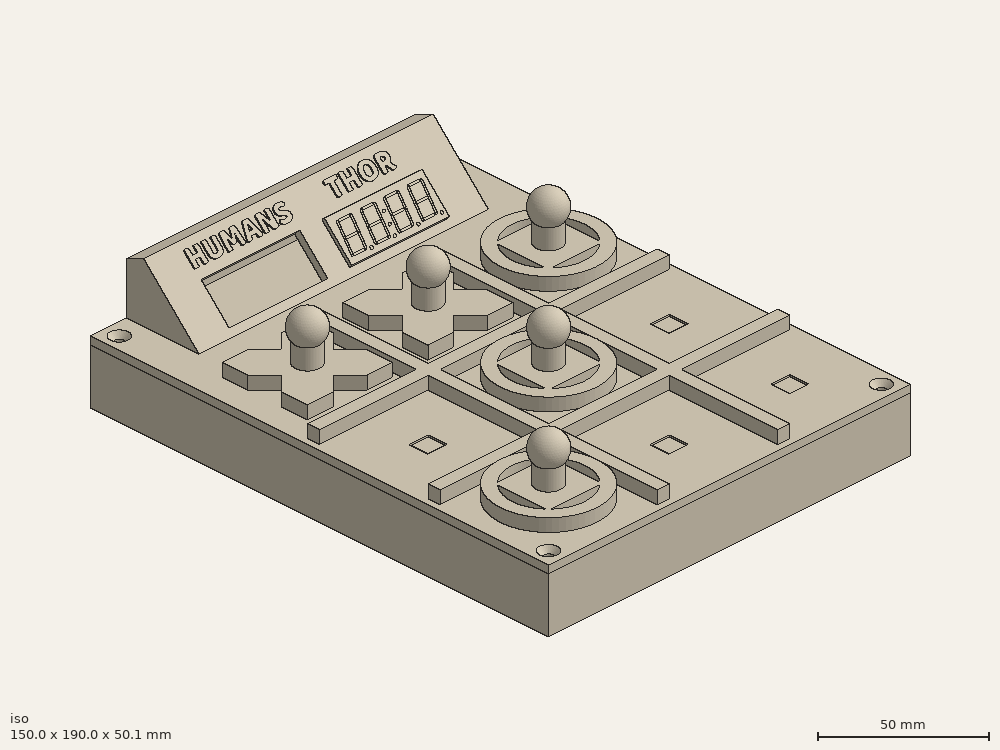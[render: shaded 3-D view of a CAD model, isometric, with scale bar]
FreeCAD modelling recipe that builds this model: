
FCSTD DOCUMENT  (FreeCAD 0.16R6707 (Git))
Label: 3enraya
License: All rights reserved
LicenseURL: http://en.wikipedia.org/wiki/All_rights_reserved
objects: Part::FeaturePython×36, Part::Feature×23, Part::MultiFuse×19, Part::Cut×14, Part::Cylinder×14, Part::Extrusion×13, Part::Box×11, Sketcher::SketchObject×3, PartDesign::Pad×3, Part::Thickness×2, Part::Chamfer×2, Part::Sphere×2, Part::Compound×2, Part::Cone×1, Part::Fillet×1, App::DocumentObjectGroup×1, Part::Prism×1, Part::Mirroring×1
note: 151 computed .brp shape members not serialized (recipe doc carries the construction recipe); baked Part::Feature solids carry a one-line shape summary decoded from their .brp

FEATURE [Part::Box] Box  label="Cube"
  Height = 14
  Length = 7
  Placement = pos=(6.5,6.5,5) rot=(0,0,1;0rad)
  Width = 7
FEATURE [Part::Box] Box001  label="Cube001"
  Height = 1.7
  Length = 20
  Placement = pos=(0,0,3.3) rot=(0,0,1;0rad)
  Width = 20
FEATURE [Part::MultiFuse] Fusion  label="Sensor"
  Shapes = -> [Box,Box001]
FEATURE [Part::Box] Box002  label="Cube002"
  Height = 3
  Length = 150
  Placement = pos=(-15,-15,16.3) rot=(0,0,1;0rad)
  Width = 190
FEATURE [Part::Box] Box003  label="Cube003"
  Height = 20
  Length = 8
  Placement = pos=(6,6,5) rot=(0,0,1;0rad)
  Width = 8
FEATURE [Part::FeaturePython] Array001  # Draft array (typed FeaturePython)
  Angle = 360
  ArrayType = 0
  Axis = (0,0,1)
  Base = -> Box003
  Center = (0,0,0)
  Fuse = false
  IntervalAxis = (0,0,0)
  IntervalX = (50,0,0)
  IntervalY = (0,50,0)
  IntervalZ = (0,0,0)
  NumberPolar = 1
  NumberX = 3
  NumberY = 3
  NumberZ = 1
FEATURE [Part::Cut] Cut
  Base = -> Box002
  Tool = -> Array001
FEATURE [Part::Box] Box004  label="Cube004"
  Height = 21.3
  Length = 150
  Placement = pos=(-15,-15,-5) rot=(0,0,1;0rad)
  Width = 190
FEATURE [Part::Thickness] Thickness
  Faces = -> Box004 [Face6]
  Intersection = false
  Join = 0
  Mode = 0
  SelfIntersection = false
  Value = -3
FEATURE [Part::Cylinder] Cylinder
  Angle = 360
  Height = 10
  Placement = pos=(18,18,0) rot=(0,0,1;0rad)
  Radius = 1
FEATURE [Part::Cylinder] Cylinder001
  Angle = 360
  Height = 10
  Placement = pos=(2,2,0) rot=(0,0,1;0rad)
  Radius = 1
FEATURE [Part::MultiFuse] Fusion001
  Shapes = -> [Cylinder001,Cylinder]
FEATURE [Part::Cut] Cut001
  Base = -> Fusion
  Tool = -> Fusion001
FEATURE [Part::FeaturePython] Array  # Draft array (typed FeaturePython)
  Angle = 360
  ArrayType = 0
  Axis = (0,0,1)
  Base = -> Cut001
  Center = (0,0,0)
  Fuse = false
  IntervalAxis = (0,0,0)
  IntervalX = (50,0,0)
  IntervalY = (0,50,0)
  IntervalZ = (0,0,0)
  NumberPolar = 1
  NumberX = 3
  NumberY = 3
  NumberZ = 1
FEATURE [Part::Cylinder] Cylinder002
  Angle = 360
  Height = 8.25
  Placement = pos=(1.11,1.11,-4.95) rot=(0,0,1;0rad)
  Radius = 1
FEATURE [Part::Cylinder] Cylinder003
  Angle = 360
  Height = 8.25
  Placement = pos=(18.89,18.89,-4.95) rot=(0,0,1;0rad)
  Radius = 1
FEATURE [Part::Cylinder] Cylinder004
  Angle = 360
  Height = 8.25
  Placement = pos=(18.89,18.89,-4.95) rot=(0,0,1;0rad)
  Radius = 3
FEATURE [Part::Cylinder] Cylinder005
  Angle = 360
  Height = 8.25
  Placement = pos=(1.11,1.11,-4.95) rot=(0,0,1;0rad)
  Radius = 3
FEATURE [Part::MultiFuse] Fusion002
  Shapes = -> [Cylinder002,Cylinder003]
FEATURE [Part::MultiFuse] Fusion003
  Shapes = -> [Cylinder005,Cylinder004]
FEATURE [Part::Box] Box005  label="Cube005"
  Height = 5
  Length = 5
  Placement = pos=(82.5,-12.5,19.3) rot=(0,0,1;0rad)
  Width = 145
FEATURE [Part::FeaturePython] Clone  label="Clone of Cube005"  # Draft clone (typed FeaturePython)
  Objects = -> [Box005]
  Placement = pos=(32.5,-12.5,19.3) rot=(0,0,1;0rad)
  Scale = (1,1,1)
FEATURE [Part::FeaturePython] Clone001  label="Clone of Cube006"  # Draft clone (typed FeaturePython)
  Objects = -> [Box005]
  Placement = pos=(132.5,82.5,19.3) rot=(0,0,1;1.5708rad)
  Scale = (1,1,1)
FEATURE [Part::FeaturePython] Clone002  label="Clone of Cube007"  # Draft clone (typed FeaturePython)
  Objects = -> [Box005]
  Placement = pos=(132.5,32.5,19.3) rot=(0,0,1;1.5708rad)
  Scale = (1,1,1)
FEATURE [Part::MultiFuse] Fusion005
  Shapes = -> [Clone002,Clone001,Clone,Box005,Cut]
FEATURE [Part::Cone] Cone
  Angle = 90
  Height = 12
  Placement = pos=(-12,-12,4.3) rot=(0,0,1;0rad)
  Radius1 = 0
  Radius2 = 10
FEATURE [Part::Box] Box006  label="Cube006"
  Height = 10
  Length = 20
  Placement = pos=(50,165,-2) rot=(0,0,1;0rad)
  Width = 10
FEATURE [Part::Fillet] Fillet
  Base = -> Box006
  Edges = 4 edges r=3: [Edge2,Edge4,Edge6,Edge8]
FEATURE [Part::FeaturePython] Clone003  label="Clone of Cone"  # Draft clone (typed FeaturePython)
  Objects = -> [Cone]
  Placement = pos=(132,-12,4.3) rot=(0,0,1;1.5708rad)
  Scale = (1,1,1)
FEATURE [Part::FeaturePython] Clone004  label="Clone of Cone001"  # Draft clone (typed FeaturePython)
  Objects = -> [Cone]
  Placement = pos=(-12,172,4.3) rot=(0,0,-1;1.5708rad)
  Scale = (1,1,1)
FEATURE [Part::FeaturePython] Clone005  label="Clone of Cone002"  # Draft clone (typed FeaturePython)
  Objects = -> [Cone]
  Placement = pos=(132,172,4.3) rot=(0,0,1;3.14159rad)
  Scale = (1,1,1)
FEATURE [Part::Cylinder] Cylinder006
  Angle = 360
  Height = 10
  Placement = pos=(-9,169,6.3) rot=(0,0,1;0rad)
  Radius = 1.6
FEATURE [Part::FeaturePython] Clone006  label="Clone of Cylinder006"  # Draft clone (typed FeaturePython)
  Objects = -> [Cylinder006]
  Placement = pos=(129,-9,6.3) rot=(0,0,1;0rad)
  Scale = (1,1,1)
FEATURE [Part::FeaturePython] Clone007  label="Clone of Cylinder007"  # Draft clone (typed FeaturePython)
  Objects = -> [Cylinder006]
  Placement = pos=(129,169,6.3) rot=(0,0,1;0rad)
  Scale = (1,1,1)
FEATURE [Part::FeaturePython] Clone008  label="Clone of Cylinder008"  # Draft clone (typed FeaturePython)
  Objects = -> [Cylinder006]
  Placement = pos=(-9,-9,6.3) rot=(0,0,1;0rad)
  Scale = (1,1,1)
FEATURE [Part::MultiFuse] Fusion007
  Shapes = -> [Clone008,Clone007,Clone006,Cylinder006]
FEATURE [Part::FeaturePython] Clone009  label="Clone of Fusion007"  # Draft clone (typed FeaturePython)
  Objects = -> [Fusion007]
  Placement = pos=(0,0,5) rot=(0,0,1;0rad)
  Scale = (1,1,1)
FEATURE [Part::Cut] Cut005
  Base = -> Fusion005
  Tool = -> Clone009
FEATURE [Part::Chamfer] Chamfer
  Base = -> Cut005
  Edges = 4 edges r=2: [Edge129,Edge146,Edge147,Edge148]
FEATURE [Part::Feature] Part__Feature  label="nano-board"
  shape: bbox 43.2 x 4.77 x 18 mm, 378 faces (baked)
FEATURE [Part::Feature] Part__Feature011  label="smt_resistor225"
  Placement = pos=(36.75,0,-12) rot=(-0.707107,0,0.707107;3.14159rad)
  shape: bbox 3.8 x 0.6 x 1.813 mm, 74 faces (baked)
FEATURE [Part::Feature] Part__Feature022  label="MINIUSBSHELL"
  Placement = pos=(38.98,1.65,-7.62) rot=(0,-1,0;1.5708rad)
  shape: bbox 9.475 x 3.822 x 11.03 mm, 243 faces (baked)
FEATURE [Part::Feature] Part__Feature023  label="MINIUSBCORE"
  Placement = pos=(32.28,1.65,-7.62) rot=(0,1,0;1.5708rad)
  shape: bbox 8.2 x 4.5 x 7.7 mm, 127 faces (baked)
FEATURE [Part::Feature] Part__Feature024  label="MINI USB CONTACT"
  Placement = pos=(33.28,1.65,-9.22) rot=(0,1,0;1.5708rad)
  shape: bbox 9.423 x 2.551 x 0.5011 mm, 31 faces (baked)
FEATURE [Part::Feature] Part__Feature025  label="MINI USB CONTACT001"
  Placement = pos=(33.28,1.65,-8.42) rot=(0,1,0;1.5708rad)
  shape: bbox 9.423 x 2.551 x 0.5011 mm, 31 faces (baked)
FEATURE [Part::Feature] Part__Feature026  label="MINI USB CONTACT002"
  Placement = pos=(33.28,1.65,-7.62) rot=(0,1,0;1.5708rad)
  shape: bbox 9.423 x 2.551 x 0.5011 mm, 31 faces (baked)
FEATURE [Part::Feature] Part__Feature027  label="MINI USB CONTACT003"
  Placement = pos=(33.28,1.65,-6.82) rot=(0,1,0;1.5708rad)
  shape: bbox 9.423 x 2.551 x 0.5011 mm, 31 faces (baked)
FEATURE [Part::Feature] Part__Feature028  label="MINI USB CONTACT004"
  Placement = pos=(33.28,1.65,-6.02) rot=(0,1,0;1.5708rad)
  shape: bbox 9.423 x 2.551 x 0.5011 mm, 31 faces (baked)
FEATURE [Part::MultiFuse] Fusion008
  Placement = pos=(3.79644,137.432,3.4) rot=(1,0,0;1.5708rad)
  Shapes = -> [Part__Feature011,Part__Feature,Part__Feature022,Part__Feature023,Part__Feature024,Part__Feature025,Part__Feature026,Part__Feature027,Part__Feature028]
FEATURE [Part::Cylinder] Cylinder007
  Angle = 360
  Height = 8.25
  Placement = pos=(18,18,-5) rot=(0,0,1;0rad)
  Radius = 3
FEATURE [Part::Cylinder] Cylinder008
  Angle = 360
  Height = 8.25
  Placement = pos=(18,18,-5) rot=(0,0,1;0rad)
  Radius = 1
FEATURE [Part::Cut] Cut006
  Base = -> Cylinder007
  Placement = pos=(23.8964,119.472,0.15) rot=(0,0,1;0rad)
  Tool = -> Cylinder008
FEATURE [Part::FeaturePython] Clone010  label="Clone of Cut006"  # Draft clone (typed FeaturePython)
  Objects = -> [Cut006]
  Placement = pos=(-16.6036,134.672,0.15) rot=(0,0,1;0rad)
  Scale = (1,1,1)
FEATURE [Part::FeaturePython] Clone011  label="Clone of Cut007"  # Draft clone (typed FeaturePython)
  Objects = -> [Cut006]
  Placement = pos=(23.8964,134.672,0.15) rot=(0,0,1;0rad)
  Scale = (1,1,1)
FEATURE [Part::FeaturePython] Clone012  label="Clone of Cut008"  # Draft clone (typed FeaturePython)
  Objects = -> [Cut006]
  Placement = pos=(-16.6036,119.472,0.15) rot=(0,0,1;0rad)
  Scale = (1,1,1)
FEATURE [Part::Box] Box007  label="Cube007"
  Height = 1.7
  Length = 21.82
  Width = 21.82
FEATURE [Part::Cylinder] Cylinder009
  Angle = 360
  Height = 2
  Placement = pos=(-0.5,-0.5,0) rot=(0,0,1;0rad)
  Radius = 0.5
FEATURE [Part::FeaturePython] Array003  # Draft array (typed FeaturePython)
  Angle = 360
  ArrayType = 0
  Axis = (0,0,1)
  Base = -> Cylinder009
  Center = (0,0,0)
  Fuse = false
  IntervalAxis = (0,0,0)
  IntervalX = (2.54,0,0)
  IntervalY = (0,2.54,0)
  IntervalZ = (0,0,0)
  NumberPolar = 1
  NumberX = 10
  NumberY = 10
  NumberZ = 1
FEATURE [Part::Cut] Cut007
  Base = -> Box007
  Tool = -> Array003
FEATURE [Part::Box] Box008  label="Cube008"
  Height = 13.3
  Length = 7
  Placement = pos=(7.43,7.43,1.7) rot=(0,0,1;0rad)
  Width = 7
FEATURE [Part::Cylinder] Cylinder010
  Angle = 360
  Height = 10
  Placement = pos=(2.04,19.82,-2.3) rot=(0,0,1;0rad)
  Radius = 1
FEATURE [Part::FeaturePython] Clone013  label="Clone of Cylinder010"  # Draft clone (typed FeaturePython)
  Objects = -> [Cylinder010]
  Placement = pos=(19.82,19.82,-2.3) rot=(0,0,1;0rad)
  Scale = (1,1,1)
FEATURE [Part::FeaturePython] Clone014  label="Clone of Cylinder011"  # Draft clone (typed FeaturePython)
  Objects = -> [Cylinder010]
  Placement = pos=(19.82,2.04,-2.3) rot=(0,0,1;0rad)
  Scale = (1,1,1)
FEATURE [Part::FeaturePython] Clone015  label="Clone of Cylinder012"  # Draft clone (typed FeaturePython)
  Objects = -> [Cylinder010]
  Placement = pos=(2.04,2.04,-2.3) rot=(0,0,1;0rad)
  Scale = (1,1,1)
FEATURE [Part::MultiFuse] Fusion010
  Shapes = -> [Clone015,Cylinder010,Clone013,Clone014]
FEATURE [Part::Cut] Cut008
  Base = -> Cut007
  Tool = -> Fusion010
FEATURE [Part::MultiFuse] Fusion011
  Placement = pos=(-0.93,-0.93,3.3) rot=(0,0,1;0rad)
  Shapes = -> [Cut008,Box008]
FEATURE [Part::FeaturePython] Array004  # Draft array (typed FeaturePython)
  Angle = 360
  ArrayType = 0
  Axis = (0,0,1)
  Base = -> Fusion011
  Center = (0,0,0)
  Fuse = false
  IntervalAxis = (0,0,0)
  IntervalX = (50,0,0)
  IntervalY = (0,50,0)
  IntervalZ = (0,0,0)
  NumberPolar = 1
  NumberX = 3
  NumberY = 3
  NumberZ = 1
FEATURE [App::DocumentObjectGroup] Group
FEATURE [Part::Box] Box009  label="Cube009"
  Height = 10
  Length = 10
  Placement = pos=(1.11,1.11,2.1) rot=(0,0,1;0rad)
  Width = 10
FEATURE [Part::FeaturePython] Clone016  label="Clone of Cube009"  # Draft clone (typed FeaturePython)
  Objects = -> [Box009]
  Placement = pos=(8.89,8.89,2.1) rot=(0,0,1;0rad)
  Scale = (1,1,1)
FEATURE [Part::MultiFuse] Fusion012
  Shapes = -> [Clone016,Box009]
FEATURE [Part::MultiFuse] Fusion013
  Shapes = -> [Fusion002,Fusion012]
FEATURE [Part::Cut] Cut009
  Base = -> Fusion003
  Tool = -> Fusion013
FEATURE [Part::FeaturePython] Array005  # Draft array (typed FeaturePython)
  Angle = 360
  ArrayType = 0
  Axis = (0,0,1)
  Base = -> Cut009
  Center = (0,0,0)
  Fuse = false
  IntervalAxis = (0,0,0)
  IntervalX = (50,0,0)
  IntervalY = (0,50,0)
  IntervalZ = (0,0,0)
  NumberPolar = 1
  NumberX = 3
  NumberY = 3
  NumberZ = 1
FEATURE [Part::MultiFuse] Fusion014
  Shapes = -> [Thickness,Array005]
FEATURE [Part::MultiFuse] Fusion015
  Shapes = -> [Fusion014,Cone,Clone004,Clone005,Clone003]
FEATURE [Part::MultiFuse] Fusion016
  Shapes = -> [Fusion015,Clone010,Clone011,Clone012,Cut006]
FEATURE [Part::Cut] Cut010
  Base = -> Fusion016
  Tool = -> Fusion007
FEATURE [Part::Cut] Cut011
  Base = -> Cut010
  Tool = -> Fillet
FEATURE [Sketcher::SketchObject] Sketch
  sketch-geometry (5):
    g0: LineSegment StartX=0 StartY=7.5 StartZ=0 EndX=17.5 EndY=7.5 EndZ=0
    g1: LineSegment StartX=17.5 StartY=7.5 StartZ=0 EndX=25 EndY=0 EndZ=0
    g2: LineSegment StartX=25 StartY=0 StartZ=0 EndX=17.5 EndY=-7.5 EndZ=0
    g3: LineSegment StartX=17.5 StartY=-7.5 StartZ=0 EndX=0 EndY=-7.5 EndZ=0
    g4: LineSegment StartX=0 StartY=7.5 StartZ=0 EndX=0 EndY=-7.5 EndZ=0
  constraints (14):
    c: PointOnObject(g0,g-2)
    c: Horizontal(g0)
    c: Coincident(g0,g1)
    c: PointOnObject(g1,g-1)
    c: Coincident(g1,g2)
    c: Coincident(g2,g3)
    c: PointOnObject(g3,g-2)
    c: Horizontal(g3)
    c: Angle(g2,g3) = 2.35619
    c: Symmetric(g2,g0,g-1)
    c: DistanceY(g2,g0) = 15
    c: DistanceX(g3,g1) = 25
    c: Coincident(g4,g0)
    c: Coincident(g4,g3)
FEATURE [PartDesign::Pad] Pad
  Length = 5
  Length2 = 100
  Sketch = -> Sketch
  Type = 0
FEATURE [Part::FeaturePython] Array006  # Draft array (typed FeaturePython)
  Angle = 360
  ArrayType = 1
  Axis = (0,0,1)
  Base = -> Pad
  Center = (0,0,0)
  Fuse = true
  IntervalAxis = (0,0,0)
  IntervalX = (1,0,0)
  IntervalY = (0,1,0)
  IntervalZ = (0,0,0)
  NumberPolar = 4
  NumberX = 2
  NumberY = 2
  NumberZ = 1
FEATURE [Part::Cylinder] Cylinder011
  Angle = 360
  Height = 15
  Radius = 5
FEATURE [Part::Sphere] Sphere
  Angle1 = -90
  Angle2 = 90
  Angle3 = 360
  Placement = pos=(0,0,17) rot=(0,0,1;0rad)
  Radius = 6.5
FEATURE [Part::MultiFuse] Fusion017  label="piezaCruz"
  Shapes = -> [Array006,Cylinder011,Sphere]
FEATURE [Sketcher::SketchObject] Sketch001
  sketch-geometry (9):
    g0: Circle CenterX=0 CenterY=0 CenterZ=0 NormalX=0 NormalY=0 NormalZ=1 Radius=20
    g1: ArcOfCircle CenterX=0 CenterY=0 CenterZ=0 NormalX=0 NormalY=0 NormalZ=1 Radius=15 StartAngle=5.55346 EndAngle=7.01291
    g2: LineSegment StartX=11.1803 StartY=10 StartZ=0 EndX=11.1803 EndY=-10 EndZ=0
    g3: ArcOfCircle CenterX=0 CenterY=0 CenterZ=0 NormalX=0 NormalY=0 NormalZ=1 Radius=15 StartAngle=2.41186 EndAngle=3.87132
    g4: LineSegment StartX=-11.1803 StartY=10 StartZ=0 EndX=-11.1803 EndY=-10 EndZ=0
    g5: ArcOfCircle CenterX=0 CenterY=0 CenterZ=0 NormalX=0 NormalY=0 NormalZ=1 Radius=15 StartAngle=0.841069 EndAngle=2.30052
    g6: ArcOfCircle CenterX=0 CenterY=0 CenterZ=0 NormalX=0 NormalY=0 NormalZ=1 Radius=15 StartAngle=3.98266 EndAngle=5.44212
    g7: LineSegment StartX=-10 StartY=-11.1803 StartZ=0 EndX=10 EndY=-11.1803 EndZ=0
    g8: LineSegment StartX=-10 StartY=11.1803 StartZ=0 EndX=10 EndY=11.1803 EndZ=0
  constraints (27):
    c: Coincident(g0,g-1)
    c: Radius(g0) = 20
    c: PointOnObject(g1,g-1)
    c: Coincident(g-1,g1)
    c: Coincident(g2,g1)
    c: Coincident(g2,g1)
    c: Vertical(g2)
    c: Coincident(g3,g-1)
    c: Coincident(g4,g3)
    c: Coincident(g4,g3)
    c: Vertical(g4)
    c: Equal(g3,g1)
    c: Equal(g4,g2)
    c: Coincident(g5,g-1)
    c: Coincident(g6,g-1)
    c: Coincident(g7,g6)
    c: Coincident(g7,g6)
    c: Horizontal(g7)
    c: Coincident(g8,g5)
    c: Coincident(g8,g5)
    c: Horizontal(g8)
    c: Equal(g8,g2)
    c: Equal(g2,g7)
    c: Equal(g1,g6)
    c: Equal(g6,g5)
    c: Radius(g3) = 15
    c: DistanceX(g8,g8) = 20
FEATURE [PartDesign::Pad] Pad001
  Length = 5
  Length2 = 100
  Sketch = -> Sketch001
  Type = 0
FEATURE [Part::Cylinder] Cylinder012
  Angle = 360
  Height = 15
  Radius = 5
FEATURE [Part::Sphere] Sphere001
  Angle1 = -90
  Angle2 = 90
  Angle3 = 360
  Placement = pos=(0,0,17) rot=(0,0,1;0rad)
  Radius = 6.5
FEATURE [Part::MultiFuse] Fusion018  label="piezaCirculo"
  Shapes = -> [Cylinder012,Pad001,Sphere001]
FEATURE [Part::FeaturePython] Clone017  label="Clone of piezaCruz"  # Draft clone (typed FeaturePython)
  Objects = -> [Fusion017]
  Placement = pos=(10,110,21.6533) rot=(0,0,1;0.785398rad)
  Scale = (1,1,1)
FEATURE [Part::FeaturePython] Clone018  label="Clone of piezaCruz001"  # Draft clone (typed FeaturePython)
  Objects = -> [Fusion017]
  Placement = pos=(60,110,21.5) rot=(0,0,1;0.785398rad)
  Scale = (1,1,1)
FEATURE [Part::FeaturePython] Clone020  label="Clone of piezaCirculo"  # Draft clone (typed FeaturePython)
  Objects = -> [Fusion018]
  Placement = pos=(10,10,21.5) rot=(0,0,1;0rad)
  Scale = (1,1,1)
FEATURE [Part::FeaturePython] Clone021  label="Clone of piezaCirculo001"  # Draft clone (typed FeaturePython)
  Objects = -> [Fusion018]
  Placement = pos=(110,110,21.5) rot=(0,0,1;0rad)
  Scale = (1,1,1)
FEATURE [Part::FeaturePython] Clone022  label="Clone of piezaCirculo002"  # Draft clone (typed FeaturePython)
  Objects = -> [Fusion018]
  Placement = pos=(60,60,21.5) rot=(0,0,1;0rad)
  Scale = (1,1,1)
FEATURE [Part::Cylinder] Cylinder013
  Angle = 360
  Height = 10
  Placement = pos=(1.11,1.11,-6.7) rot=(0,0,1;0rad)
  Radius = 1.65
FEATURE [Part::FeaturePython] Clone023  label="Clone of Cylinder013"  # Draft clone (typed FeaturePython)
  Objects = -> [Cylinder013]
  Placement = pos=(18.89,18.89,-6.7) rot=(0,0,1;0rad)
  Scale = (1,1,1)
FEATURE [Part::Prism] Prism001  label="M3Nut"
  Circumradius = 3.35
  Height = 5.5
  Placement = pos=(1.11,1.11,-8.7) rot=(0,0,1;0rad)
  Polygon = 6
FEATURE [Part::FeaturePython] Clone024  label="Clone of M3Nut"  # Draft clone (typed FeaturePython)
  Objects = -> [Prism001]
  Placement = pos=(18.89,18.89,-8.7) rot=(0,0,1;0rad)
  Scale = (1,1,1)
FEATURE [Part::MultiFuse] Fusion019
  Shapes = -> [Prism001,Clone024,Clone023,Cylinder013]
FEATURE [Part::FeaturePython] Array007  # Draft array (typed FeaturePython)
  Angle = 360
  ArrayType = 0
  Axis = (0,0,1)
  Base = -> Fusion019
  Center = (0,0,0)
  Fuse = false
  IntervalAxis = (0,0,0)
  IntervalX = (50,0,0)
  IntervalY = (0,50,0)
  IntervalZ = (0,0,0)
  NumberPolar = 1
  NumberX = 3
  NumberY = 3
  NumberZ = 1
FEATURE [Part::Cut] Cut012
  Base = -> Cut011
  Tool = -> Array007
FEATURE [Part::Feature] Part__Feature029  label="Cc56-12"
  shape: bbox 50 x 19 x 10.5 mm, 226 faces (baked)
FEATURE [Part::FeaturePython] Clone025  label="Clone of Cc56-12"  # Draft clone (typed FeaturePython)
  Objects = -> [Part__Feature029]
  Placement = pos=(35,157,23) rot=(1,0,0;0.785398rad)
  Scale = (0.81,0.842,0.875)
FEATURE [Part::FeaturePython] Clone026  label="Clone of Clone of Cc56-12"  # Draft clone (typed FeaturePython)
  Objects = -> [Clone025]
  Placement = pos=(85,157,23) rot=(1,0,0;0.785398rad)
  Scale = (1,1,1)
FEATURE [Sketcher::SketchObject] Sketch002
  Placement = pos=(0,0,0) rot=(0.57735,0.57735,0.57735;2.0944rad)
  sketch-geometry (3):
    g0: LineSegment StartX=0 StartY=0 StartZ=0 EndX=30 EndY=30 EndZ=0
    g1: LineSegment StartX=30 StartY=30 StartZ=0 EndX=30 EndY=0 EndZ=0
    g2: LineSegment StartX=30 StartY=0 StartZ=0 EndX=0 EndY=0 EndZ=0
  constraints (8):
    c: Coincident(g0,g1)
    c: Vertical(g1)
    c: Coincident(g1,g2)
    c: Coincident(g2,g0)
    c: Horizontal(g2)
    c: Angle(g2,g0) = 0.785398
    c: DistanceY(g1,g1) = 30
    c: Coincident(g0,g-1)
FEATURE [PartDesign::Pad] Pad002
  Length = 120
  Length2 = 100
  Placement = pos=(0,0,0) rot=(0.57735,0.57735,0.57735;2.0944rad)
  Sketch = -> Sketch002
  Type = 0
FEATURE [Part::FeaturePython] Clone027  label="Clone of Pad002"  # Draft clone (typed FeaturePython)
  Objects = -> [Pad002]
  Placement = pos=(0,145,19.3) rot=(0.57735,0.57735,0.57735;2.0944rad)
  Scale = (1,1,1)
FEATURE [Part::Chamfer] Chamfer001
  Base = -> Clone027
  Edges = 1 edges r=10: [Edge2]
FEATURE [Part::Box] Box010  label="Cube010"
  Height = 16.4
  Length = 40.9
  Placement = pos=(14.55,146.252,22.1515) rot=(-1,0,0;0.785398rad)
  Width = 10
FEATURE [Part::Thickness] Thickness001
  Faces = -> Chamfer001 [Face4]
  Intersection = false
  Join = 0
  Mode = 0
  SelfIntersection = false
  Value = -3
FEATURE [Part::Mirroring] Part__Mirroring  label="Cube010 (Mirror #1)"
  Base = (60,0,0)
  Normal = (1,0,0)
  Source = -> Box010
FEATURE [Part::MultiFuse] Fusion020
  Shapes = -> [Box010,Part__Mirroring]
FEATURE [Part::Cut] Cut013
  Base = -> Thickness001
  Tool = -> Fusion020
FEATURE [Part::Feature] path4495
  shape: bbox 5.736 x 6.562 x 2e-07 mm, 0 faces, 0 solids (baked)
FEATURE [Part::Feature] path4497
  shape: bbox 5.715 x 6.678 x 2e-07 mm, 0 faces, 0 solids (baked)
FEATURE [Part::Feature] path4499
  shape: bbox 7.398 x 6.541 x 2e-07 mm, 0 faces, 0 solids (baked)
FEATURE [Part::Feature] path4501
  shape: bbox 6.212 x 6.625 x 2e-07 mm, 0 faces, 0 solids (baked)
FEATURE [Part::Feature] path4501001
  shape: bbox 1.312 x 2.096 x 2e-07 mm, 0 faces, 0 solids (baked)
FEATURE [Part::Feature] path4503
  shape: bbox 5.81 x 6.593 x 2e-07 mm, 0 faces, 0 solids (baked)
FEATURE [Part::Feature] path4505
  shape: bbox 5.091 x 6.763 x 2e-07 mm, 0 faces, 0 solids (baked)
FEATURE [Part::Feature] path4507
  shape: bbox 5.482 x 6.498 x 2e-07 mm, 0 faces, 0 solids (baked)
FEATURE [Part::Feature] path4509
  shape: bbox 5.736 x 6.562 x 2e-07 mm, 0 faces, 0 solids (baked)
FEATURE [Part::Feature] path4511
  shape: bbox 6.699 x 6.805 x 2e-07 mm, 0 faces, 0 solids (baked)
FEATURE [Part::Feature] path4511001
  shape: bbox 2.889 x 3.821 x 2e-07 mm, 0 faces, 0 solids (baked)
FEATURE [Part::Feature] path4513
  shape: bbox 5.44 x 6.678 x 2e-07 mm, 0 faces, 0 solids (baked)
FEATURE [Part::Feature] path4513001
  shape: bbox 1.545 x 1.63 x 2e-07 mm, 0 faces, 0 solids (baked)
FEATURE [Part::Extrusion] Extrude
  Base = -> path4495
  Dir = (0,0,1)
  Solid = true
FEATURE [Part::Extrusion] Extrude001
  Base = -> path4497
  Dir = (0,0,1)
  Solid = true
FEATURE [Part::Extrusion] Extrude002
  Base = -> path4499
  Dir = (0,0,1)
  Solid = true
FEATURE [Part::Extrusion] Extrude003
  Base = -> path4501
  Dir = (0,0,1)
  Solid = true
FEATURE [Part::Extrusion] Extrude004
  Base = -> path4501001
  Dir = (0,0,1)
  Solid = true
FEATURE [Part::Extrusion] Extrude005
  Base = -> path4503
  Dir = (0,0,1)
  Solid = true
FEATURE [Part::Extrusion] Extrude006
  Base = -> path4505
  Dir = (0,0,1)
  Solid = true
FEATURE [Part::Cut] Cut014
  Base = -> Extrude003
  Tool = -> Extrude004
FEATURE [Part::Compound] Compound  label="HumansText"
  Links = -> [Extrude006,Extrude005,Extrude002,Extrude,Extrude001,Cut014]
FEATURE [Part::Extrusion] Extrude007
  Base = -> path4507
  Dir = (0,0,1)
  Solid = true
FEATURE [Part::Extrusion] Extrude008
  Base = -> path4509
  Dir = (0,0,1)
  Solid = true
FEATURE [Part::Extrusion] Extrude009
  Base = -> path4511
  Dir = (0,0,1)
  Solid = true
FEATURE [Part::Extrusion] Extrude010
  Base = -> path4511001
  Dir = (0,0,1)
  Solid = true
FEATURE [Part::Extrusion] Extrude011
  Base = -> path4513
  Dir = (0,0,1)
  Solid = true
FEATURE [Part::Extrusion] Extrude012
  Base = -> path4513001
  Dir = (0,0,1)
  Solid = true
FEATURE [Part::Cut] Cut015
  Base = -> Extrude011
  Tool = -> Extrude012
FEATURE [Part::Cut] Cut016
  Base = -> Extrude009
  Tool = -> Extrude010
FEATURE [Part::Compound] Compound001  label="ThorText"
  Links = -> [Cut016,Cut015,Extrude007,Extrude008]
FEATURE [Part::FeaturePython] Clone028  label="Clone of HumansText"  # Draft clone (typed FeaturePython)
  Objects = -> [Compound]
  Placement = pos=(-32,231.5,105) rot=(1,0,0;0.785398rad)
  Scale = (1,1,1)
FEATURE [Part::FeaturePython] Clone029  label="Clone of ThorText"  # Draft clone (typed FeaturePython)
  Objects = -> [Compound001]
  Placement = pos=(26,241.532,115.032) rot=(1,0,0;0.785398rad)
  Scale = (1,1,1)
FEATURE [Part::MultiFuse] Fusion021
  Shapes = -> [Cut013,Clone029,Clone028]
